# Revit family: 35-72-005-DN100
name_source: partatom
category: Pipe Accessories
units: mm (PartAtom-declared; Revit-internal decimal feet)

## family parameters
Always vertical = Yes
Cut with Voids When Loaded = No
Part Type = Valve - Breaks Into
Round Connector Dimension = Use Diameter
Shared = No
Work Plane-Based = No

## types (14) — shared parameters
Bottom_Chamfer = 110 mm  [stored 0.360892 ft]
Bottom_Flange_Dia = 110 mm  [stored 0.360892 ft]
Bottom_Flange_Thickness = 20 mm  [stored 0.0656168 ft]
DN = 100 mm  [stored 0.328084 ft]
DN100-0750 = 35-125-72-072000
DN100-1000 = 35-125-72-082000
DN100-1250 = 35-125-72-092000
DN100-1500 = 35-125-72-102000
DN100-1750 = 35-125-72-112000
DN100-2000 = 35-125-72-122000
DN100-2250 = 35-125-72-132000
DN100-2500 = 35-125-72-142000
DN100-2750 = 35-125-72-152000
DN100-3000 = 35-125-72-162000
DN100-3250 = 35-125-72-172000
DN100-3500 = 35-125-72-182000
DN100-3750 = 35-125-72-192000
DN100-4000 = 35-125-72-202000
Description_ = AVK UNDERGROUND FIRE HYDRANT, GOST
Fillet = 40 mm  [stored 0.131234 ft]
Flange_width = 180 mm  [stored 0.590551 ft]
Flange_width_2 = 90 mm  [stored 0.295276 ft]
Search_Table = 35-72-005-DN100
Top_Flange = 150 mm  [stored 0.492126 ft]
Top_Flange_Thickness = 40 mm  [stored 0.131234 ft]
Top_Height_reference = 115 mm  [stored 0.377297 ft]

## per-type parameters (varying)
| type | Flange_width_3 | H3 | H6 | Nominal Diameter (DN) | URL product pages |
| DN100-0750 | 100 mm  [stored 0.328084 ft] | 750 mm  [stored 2.46063 ft] | 335 mm  [stored 1.09908 ft] | 125.01 mm  [stored 0.410138 ft] | https://www.avkvalves.com
https://www.avkvalves.com
https://www.avkvalves.com
https://www.avkvalves.com |
| DN100-1000 | 100 mm  [stored 0.328084 ft] | 1000 mm  [stored 3.28084 ft] | 585 mm  [stored 1.91929 ft] | 125.02 mm  [stored 0.410171 ft] | https://www.avkvalves.com
https://www.avkvalves.comhttps:
https://www.avkvalves.com
https://www.avkvalves.com
https://www.avkvalves.com |
| DN100-1250 | 100 mm  [stored 0.328084 ft] | 1250 mm  [stored 4.10105 ft] | 835 mm | 125.03 mm  [stored 0.410203 ft] | https://www.avkvalves.com
https://www.avkvalves.com
https://www.avkvalves.com
https://www.avkvalves.com
https://www.avkvalves.com |
| DN100-1500 | 180 mm  [stored 0.590551 ft] | 1500 mm  [stored 4.92126 ft] | 1085 mm  [stored 3.55971 ft] | 125.04 mm  [stored 0.410236 ft] | https://www.avkvalves.com |
| DN100-1750 | 180 mm  [stored 0.590551 ft] | 1750 mm  [stored 5.74147 ft] | 1085 mm  [stored 3.55971 ft] | 125.05 mm  [stored 0.410269 ft] | https://www.avkvalves.com |
| DN100-2000 | 180 mm  [stored 0.590551 ft] | 2000 mm  [stored 6.56168 ft] | 1085 mm  [stored 3.55971 ft] | 125.06 mm  [stored 0.410302 ft] | https://www.avkvalves.com |
| DN100-2250 | 180 mm  [stored 0.590551 ft] | 2250 mm  [stored 7.38189 ft] | 1085 mm  [stored 3.55971 ft] | 125.07 mm  [stored 0.410335 ft] | https://www.avkvalves.com |
| DN100-2500 | 180 mm  [stored 0.590551 ft] | 2500 mm  [stored 8.2021 ft] | 1085 mm  [stored 3.55971 ft] | 125.08 mm  [stored 0.410367 ft] | https://www.avkvalves.com |
| DN100-2750 | 180 mm  [stored 0.590551 ft] | 2750 mm  [stored 9.02231 ft] | 1085 mm  [stored 3.55971 ft] | 125.09 mm  [stored 0.4104 ft] | https://www.avkvalves.com |
| DN100-3000 | 180 mm  [stored 0.590551 ft] | 3000 mm  [stored 9.84252 ft] | 1085 mm  [stored 3.55971 ft] | 125.1 mm  [stored 0.410433 ft] | https://www.avkvalves.com |
| DN100-3250 | 180 mm  [stored 0.590551 ft] | 3250 mm  [stored 10.6627 ft] | 1085 mm  [stored 3.55971 ft] | 125.11 mm  [stored 0.410466 ft] | https://www.avkvalves.com |
| DN100-3500 | 180 mm  [stored 0.590551 ft] | 3500 mm  [stored 11.4829 ft] | 1085 mm  [stored 3.55971 ft] | 125.12 mm  [stored 0.410499 ft] | https://www.avkvalves.com |
| DN100-4000 | 180 mm  [stored 0.590551 ft] | 4000 mm  [stored 13.1234 ft] | 1085 mm  [stored 3.55971 ft] | 125.14 mm  [stored 0.410564 ft] | https://www.avkvalves.com |
| DN100-3750 | 180 mm  [stored 0.590551 ft] | 3750 mm  [stored 12.3031 ft] | 1085 mm  [stored 3.55971 ft] | 125.13 mm  [stored 0.410531 ft] | https://www.avkvalves.com |

note: [stored X ft] marks values corroborated as IEEE doubles in the binary element streams (Revit-internal decimal feet)

## geometry (parser evidence)
native form markers: Sweep x6
no freeform markers — native parametric forms only
